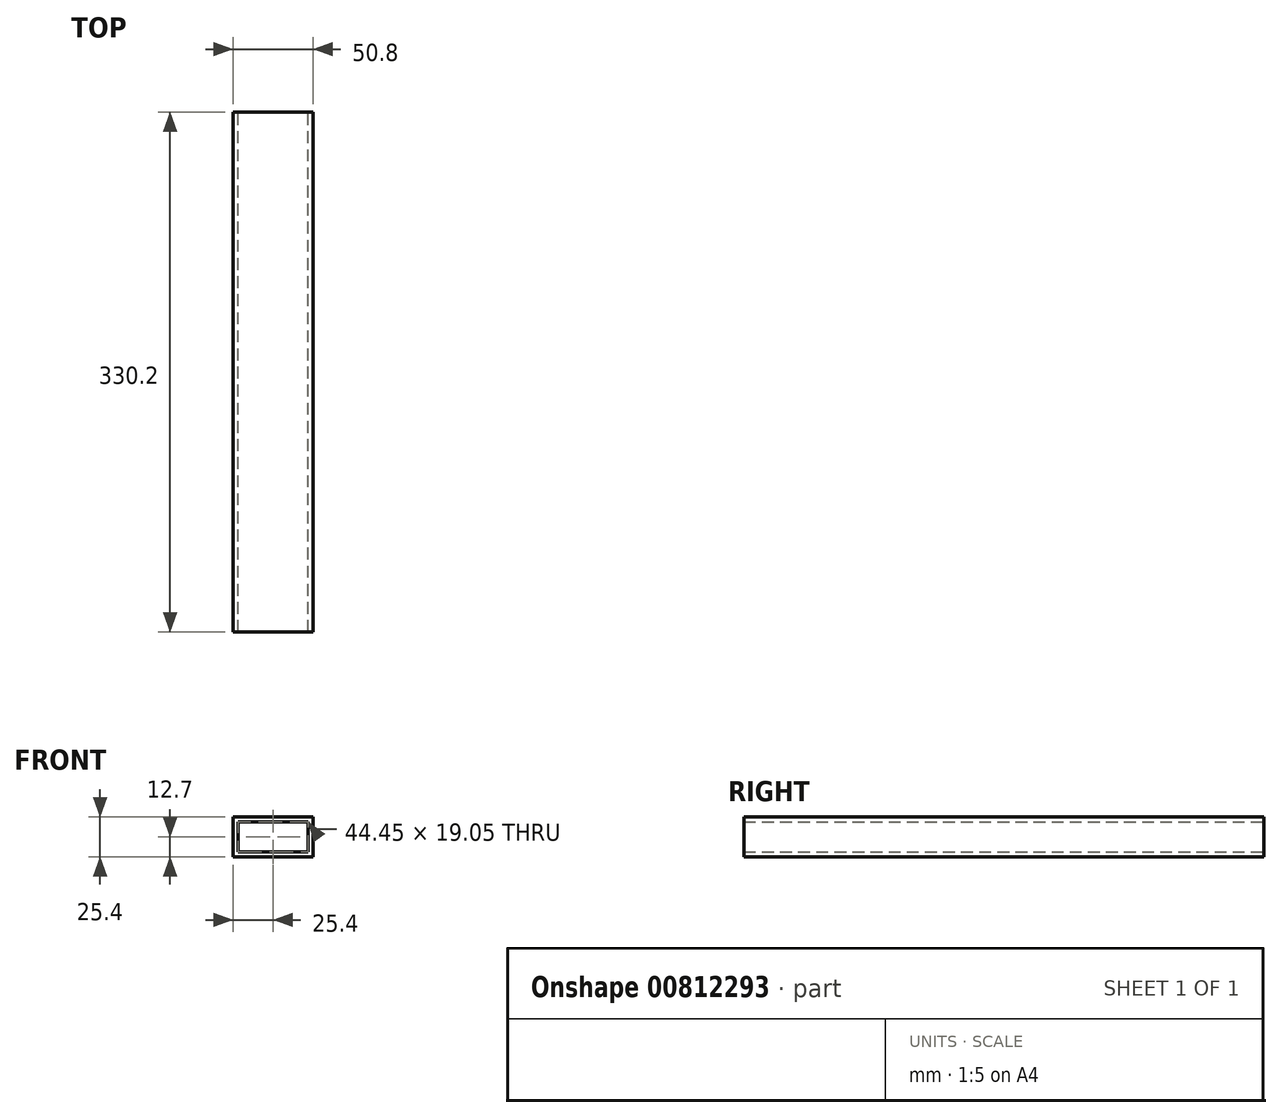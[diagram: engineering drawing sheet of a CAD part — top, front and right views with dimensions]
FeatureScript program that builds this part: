
annotation { "Feature Type Name" : "Feature", "Feature Type Description" : "" }
export const myFeature = defineFeature(function(context is Context, id is Id, definition is map)
    precondition{}
    {
        {
            var Q0;
            Q0=qCreatedBy(makeId("Front.planeOp"),FACE);
            var sketch = newSketch(context, id + "F0", { "sketchPlane" : qUnion([Q0])});
            skLineSegment(sketch, "E0.bottom", {"start": v(22.23, 9.53) * mm, "end": v(-22.23, 9.53) * mm});
            skLineSegment(sketch, "E0.top", {"start": v(22.23, -9.53) * mm, "end": v(-22.23, -9.53) * mm});
            skLineSegment(sketch, "E0.left", {"start": v(22.23, 9.53) * mm, "end": v(22.23, -9.53) * mm});
            skLineSegment(sketch, "E0.right", {"start": v(-22.23, 9.53) * mm, "end": v(-22.23, -9.53) * mm});
            skPoint(sketch, "E0.middle", {"position": v(0, 0) * mm});
            skLineSegment(sketch, "E1.bottom", {"start": v(25.4, 12.7) * mm, "end": v(-25.4, 12.7) * mm});
            skLineSegment(sketch, "E1.top", {"start": v(25.4, -12.7) * mm, "end": v(-25.4, -12.7) * mm});
            skLineSegment(sketch, "E1.left", {"start": v(25.4, 12.7) * mm, "end": v(25.4, -12.7) * mm});
            skLineSegment(sketch, "E1.right", {"start": v(-25.4, 12.7) * mm, "end": v(-25.4, -12.7) * mm});
            skSolve(sketch);
        }
        {
            var Q0;
            Q0=makeQuery(id+"F0.imprint","IMPRINT",FACE,{"disambiguationData":[TD([[makeQuery(id+"F0.imprint","IMPRINT",EDGE,{"derivedFrom":sQuery(id+"F0.wireOp",EDGE,"E0.bottom")}),-1.0]])]});
            extrude(context, id + "F1", {"entities" : qUnion([Q0]), "endBound" : BoundingType.SYMMETRIC, "depth" : 330.2 * mm, "offsetDistance" : 25.4 * mm});
        }
    });
